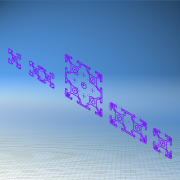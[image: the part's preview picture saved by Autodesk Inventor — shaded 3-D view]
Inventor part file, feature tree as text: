
AUTODESK INVENTOR PART (.ipt)
format: ipt  version: 2020.2 (Build 242310000, 310)  size: 398,848 bytes
history: native  units: mm
features: sketch x1
ambient origin geometry x8: Origin, YZ Plane, XZ Plane, XY Plane, X Axis, Y Axis, Z Axis, Center Point
feature tree (1):
  sketch  "Sketch1"  dims[d5=40.0mm d6=360.0deg d7=1.5mm d17=40.0mm d18=9.9mm d19=4.0mm d20=4.0mm d21=0.1mm d22=0.1mm d23=9.9mm d24=0.1mm d25=0.1mm d27=40.0mm d29=40.0mm d34=40.0mm d36=40.0mm d37=360.0deg]
